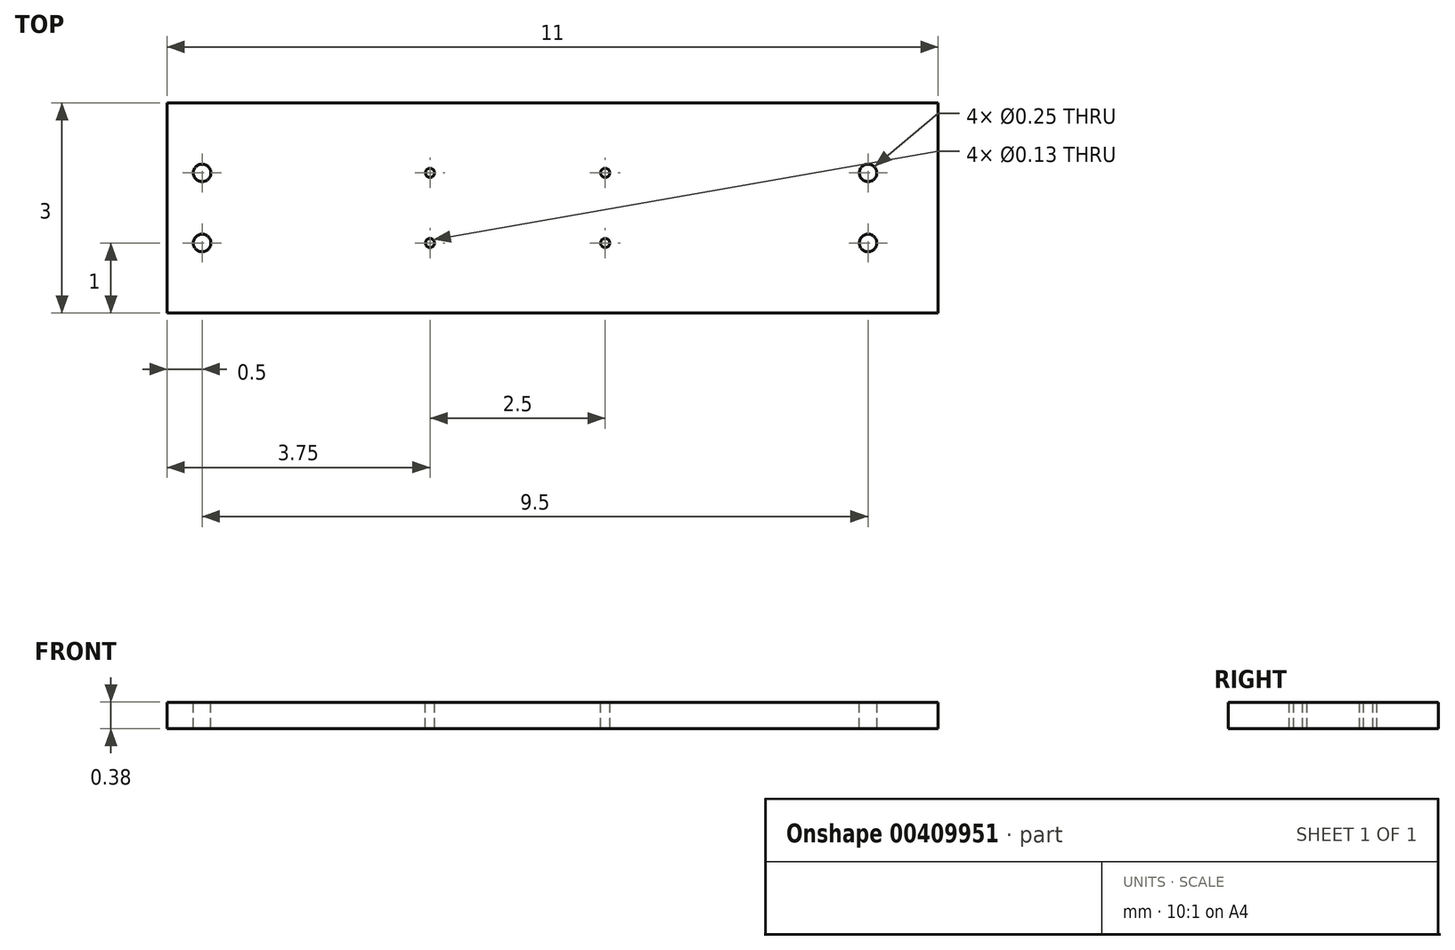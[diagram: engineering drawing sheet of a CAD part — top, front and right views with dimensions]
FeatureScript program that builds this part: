
annotation { "Feature Type Name" : "Feature", "Feature Type Description" : "" }
export const myFeature = defineFeature(function(context is Context, id is Id, definition is map)
    precondition{}
    {
        {
            var Q0;
            Q0=qCreatedBy(makeId("Top.planeOp"),FACE);
            var sketch = newSketch(context, id + "F0", { "sketchPlane" : qUnion([Q0])});
            skLineSegment(sketch, "E0.bottom", {"start": v(0, 1.5) * mm, "end": v(11, 1.5) * mm});
            skLineSegment(sketch, "E0.top", {"start": v(0, -1.5) * mm, "end": v(11, -1.5) * mm});
            skLineSegment(sketch, "E0.left", {"start": v(0, 1.5) * mm, "end": v(0, -1.5) * mm});
            skLineSegment(sketch, "E0.right", {"start": v(11, 1.5) * mm, "end": v(11, -1.5) * mm});
            skSolve(sketch);
        }
        {
            var Q0;
            Q0=makeQuery(id+"F0.imprint","IMPRINT",FACE,{"disambiguationData":[TD([[makeQuery(id+"F0.imprint","IMPRINT",EDGE,{"derivedFrom":sQuery(id+"F0.wireOp",EDGE,"E0.bottom")}),-1.0]])]});
            extrude(context, id + "F1", {"entities" : qUnion([Q0]), "depth" : 0.38 * mm});
        }
        {
            var Q0;
            Q0=makeQuery(id+"F1.opExtrude","CAP_FACE",FACE,{"disambiguationData":[OSD([sQuery(id+"F0.wireOp",EDGE,"E0.bottom"),sQuery(id+"F0.wireOp",EDGE,"E0.top"),sQuery(id+"F0.wireOp",EDGE,"E0.left"),sQuery(id+"F0.wireOp",EDGE,"E0.right")])],"isStart":false});
            var sketch = newSketch(context, id + "F2", { "sketchPlane" : qUnion([Q0])});
            skPoint(sketch, "E1", {"position": v(0.5, 0.5) * mm});
            skPoint(sketch, "E2", {"position": v(0.5, -0.5) * mm});
            skPoint(sketch, "E3", {"position": v(10, -0.5) * mm});
            skPoint(sketch, "E4", {"position": v(10, 0.5) * mm});
            skSolve(sketch);
        }
        {
            var Q0;
            Q0=sQuery(id+"F2.wireOp",VERTEX,"E1");
            var Q1;
            Q1=sQuery(id+"F2.wireOp",VERTEX,"E2");
            var Q2;
            Q2=sQuery(id+"F2.wireOp",VERTEX,"E3");
            var Q3;
            Q3=sQuery(id+"F2.wireOp",VERTEX,"E4");
            var Q4;
            Q4=makeQuery(id+"F1.opExtrude","SWEPT_BODY",BODY,{"disambiguationData":[OSD([sQuery(id+"F0.wireOp",EDGE,"E0.bottom"),sQuery(id+"F0.wireOp",EDGE,"E0.top"),sQuery(id+"F0.wireOp",EDGE,"E0.left"),sQuery(id+"F0.wireOp",EDGE,"E0.right")])]});
            hole(context, id + "F3", {"style" : HoleStyle.SIMPLE, "endStyle" : HoleEndStyle.BLIND, "holeDiameter" : 0.25 * mm, "holeDepth" : 12 * mm, "isTappedThrough" : true, "tappedDepth" : 12 * mm, "tapClearance" : 3, "locations" : qUnion([Q0, Q1, Q2, Q3]), "scope" : qUnion([Q4])});
        }
        {
            var Q0;
            Q0=makeQuery(id+"F1.opExtrude","CAP_FACE",FACE,{"disambiguationData":[OSD([sQuery(id+"F0.wireOp",EDGE,"E0.bottom"),sQuery(id+"F0.wireOp",EDGE,"E0.top"),sQuery(id+"F0.wireOp",EDGE,"E0.left"),sQuery(id+"F0.wireOp",EDGE,"E0.right")])],"isStart":false});
            var sketch = newSketch(context, id + "F4", { "sketchPlane" : qUnion([Q0])});
            skPoint(sketch, "E5", {"position": v(3.75, 0.5) * mm});
            skPoint(sketch, "E6", {"position": v(6.25, 0.5) * mm});
            skPoint(sketch, "E7", {"position": v(6.25, -0.5) * mm});
            skPoint(sketch, "E8", {"position": v(3.75, -0.5) * mm});
            skSolve(sketch);
        }
        {
            var Q0;
            Q0=sQuery(id+"F4.wireOp",VERTEX,"E5");
            var Q1;
            Q1=sQuery(id+"F4.wireOp",VERTEX,"E8");
            var Q2;
            Q2=sQuery(id+"F4.wireOp",VERTEX,"E7");
            var Q3;
            Q3=sQuery(id+"F4.wireOp",VERTEX,"E6");
            var Q4;
            Q4=makeQuery(id+"F1.opExtrude","SWEPT_BODY",BODY,{"disambiguationData":[OSD([sQuery(id+"F0.wireOp",EDGE,"E0.bottom"),sQuery(id+"F0.wireOp",EDGE,"E0.top"),sQuery(id+"F0.wireOp",EDGE,"E0.left"),sQuery(id+"F0.wireOp",EDGE,"E0.right")])]});
            hole(context, id + "F5", {"style" : HoleStyle.SIMPLE, "endStyle" : HoleEndStyle.BLIND, "holeDiameter" : 0.13 * mm, "holeDepth" : 12 * mm, "isTappedThrough" : true, "tappedDepth" : 12 * mm, "tapClearance" : 3, "locations" : qUnion([Q0, Q1, Q2, Q3]), "scope" : qUnion([Q4])});
        }
    });
